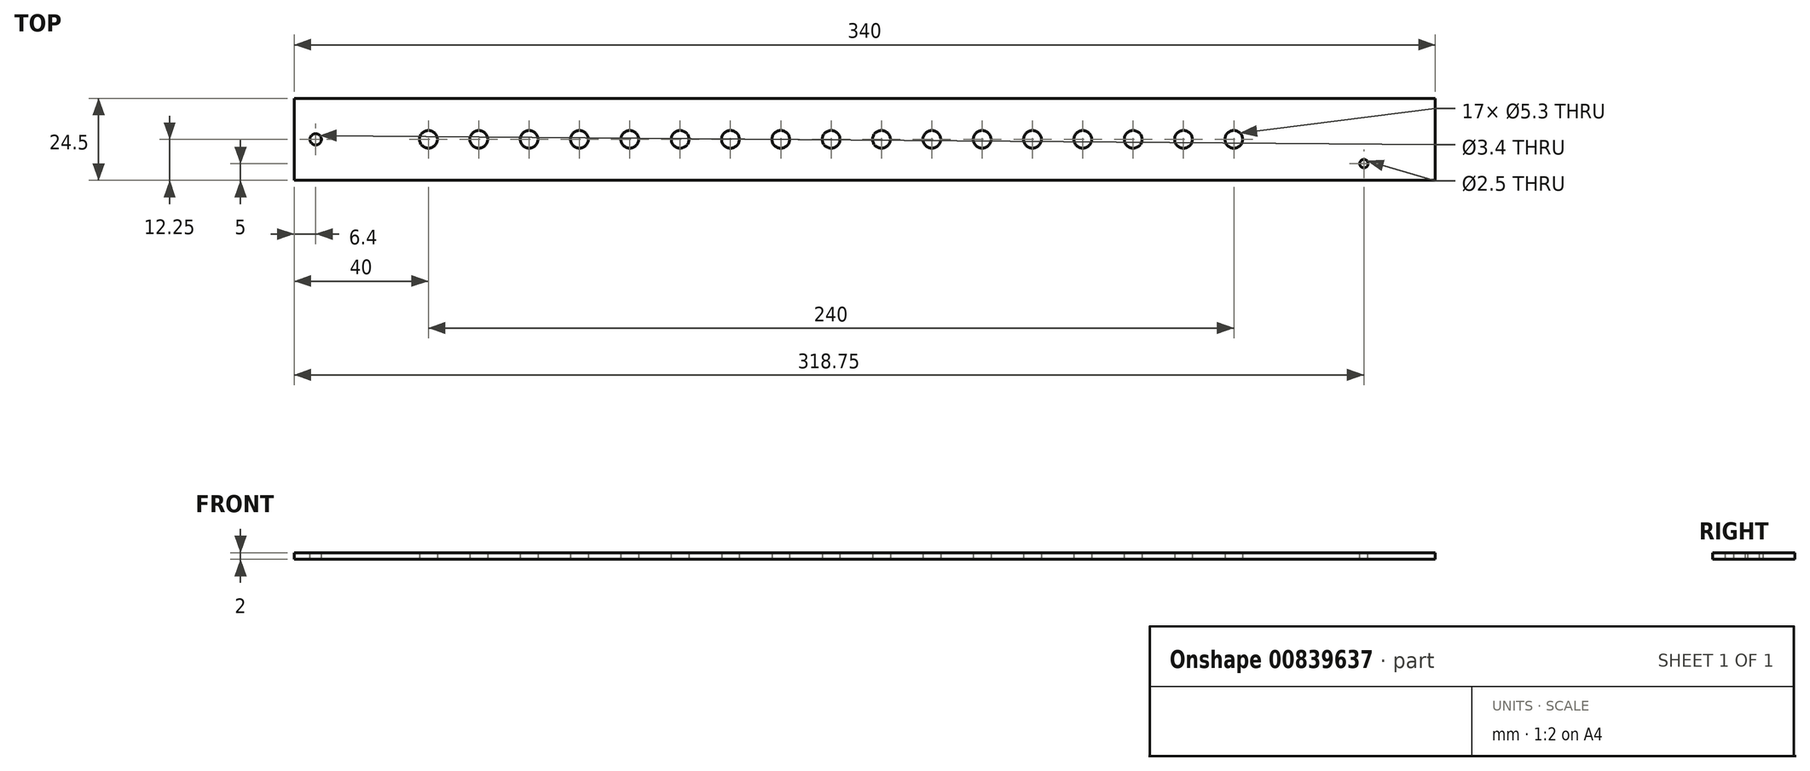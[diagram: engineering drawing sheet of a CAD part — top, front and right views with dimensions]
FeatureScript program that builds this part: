
annotation { "Feature Type Name" : "Feature", "Feature Type Description" : "" }
export const myFeature = defineFeature(function(context is Context, id is Id, definition is map)
    precondition{}
    {
        {
            var Q0;
            Q0=qCreatedBy(makeId("Top.planeOp"),FACE);
            var sketch = newSketch(context, id + "F0", { "sketchPlane" : qUnion([Q0])});
            skLineSegment(sketch, "E0.bottom", {"start": v(150, -12.25) * mm, "end": v(-150, -12.25) * mm});
            skLineSegment(sketch, "E0.top", {"start": v(150, 12.25) * mm, "end": v(-150, 12.25) * mm});
            skLineSegment(sketch, "E0.left", {"start": v(150, -12.25) * mm, "end": v(150, 12.25) * mm});
            skLineSegment(sketch, "E0.right", {"start": v(-150, -12.25) * mm, "end": v(-150, 12.25) * mm});
            skPoint(sketch, "E0.middle", {"position": v(0, 0) * mm});
            skCircle(sketch, "E1.1.0.0", {"center": v(-120, 0) * mm, "radius": 2.65 * mm});
            skCircle(sketch, "E1.2.0.0", {"center": v(-105, 0) * mm, "radius": 2.65 * mm});
            skCircle(sketch, "E1.3.0.0", {"center": v(-90, 0) * mm, "radius": 2.65 * mm});
            skCircle(sketch, "E1.4.0.0", {"center": v(-75, 0) * mm, "radius": 2.65 * mm});
            skCircle(sketch, "E1.5.0.0", {"center": v(-60, 0) * mm, "radius": 2.65 * mm});
            skCircle(sketch, "E1.6.0.0", {"center": v(-45, 0) * mm, "radius": 2.65 * mm});
            skCircle(sketch, "E1.7.0.0", {"center": v(-30, 0) * mm, "radius": 2.65 * mm});
            skCircle(sketch, "E1.8.0.0", {"center": v(-15, 0) * mm, "radius": 2.65 * mm});
            skCircle(sketch, "E1.9.0.0", {"center": v(0, 0) * mm, "radius": 2.65 * mm});
            skCircle(sketch, "E1.10.0.0", {"center": v(15, 0) * mm, "radius": 2.65 * mm});
            skCircle(sketch, "E1.11.0.0", {"center": v(30, 0) * mm, "radius": 2.65 * mm});
            skCircle(sketch, "E1.12.0.0", {"center": v(45, 0) * mm, "radius": 2.65 * mm});
            skCircle(sketch, "E1.13.0.0", {"center": v(60, 0) * mm, "radius": 2.65 * mm});
            skCircle(sketch, "E1.14.0.0", {"center": v(75, 0) * mm, "radius": 2.65 * mm});
            skCircle(sketch, "E1.15.0.0", {"center": v(90, 0) * mm, "radius": 2.65 * mm});
            skCircle(sketch, "E1.16.0.0", {"center": v(105, 0) * mm, "radius": 2.65 * mm});
            skCircle(sketch, "E1.17.0.0", {"center": v(120, 0) * mm, "radius": 2.65 * mm});
            skLineSegment(sketch, "E1.direction1", {"start": v(-135, 0) * mm, "end": v(-120, 0) * mm, "construction": true});
            skSolve(sketch);
        }
        {
            var Q0;
            Q0=makeQuery(id+"F0.imprint","IMPRINT",FACE,{"disambiguationData":[TD([[makeQuery(id+"F0.imprint","IMPRINT",EDGE,{"derivedFrom":sQuery(id+"F0.wireOp",EDGE,"E0.bottom")}),-1.0]])]});
            extrude(context, id + "F1", {"entities" : qUnion([Q0]), "depth" : 2 * mm, "offsetDistance" : 25 * mm});
        }
        {
            var Q0;
            Q0=makeQuery(id+"F1.opExtrude","SWEPT_FACE",FACE,{"disambiguationData":[OSD([sQuery(id+"F0.wireOp",EDGE,"E0.right")])]});
            extrude(context, id + "F2", {"entities" : qUnion([Q0]), "operationType" : NewBodyOperationType.ADD, "depth" : 10 * mm, "offsetDistance" : 25 * mm});
        }
        {
            var Q0;
            Q0=makeQuery(id+"F1.opExtrude","SWEPT_FACE",FACE,{"disambiguationData":[OSD([sQuery(id+"F0.wireOp",EDGE,"E0.left")])]});
            extrude(context, id + "F3", {"entities" : qUnion([Q0]), "operationType" : NewBodyOperationType.ADD, "depth" : 30 * mm, "offsetDistance" : 25 * mm});
        }
        {
            var Q0;
            {var subQ0=sQuery(id+"F0.wireOp",EDGE,"E0.left");var subQ1=sQuery(id+"F0.wireOp",EDGE,"E0.right");Q0=makeQuery(id+"F3.boolean.opBoolean","MERGE",FACE,{"derivedFrom":[makeQuery(id+"F2.boolean.opBoolean","MERGE",FACE,{"derivedFrom":[makeQuery(id+"F1.opExtrude","CAP_FACE",FACE,{"disambiguationData":[OSD([sQuery(id+"F0.wireOp",EDGE,"E0.bottom"),sQuery(id+"F0.wireOp",EDGE,"E0.top"),subQ0,subQ1,sQuery(id+"F0.wireOp",EDGE,"LckrCdrf-Oz9b-iWqB-HkfW-gHpTPrbceAxr"),sQuery(id+"F0.wireOp",EDGE,"E1.1.0.0"),sQuery(id+"F0.wireOp",EDGE,"E1.2.0.0"),sQuery(id+"F0.wireOp",EDGE,"E1.3.0.0"),sQuery(id+"F0.wireOp",EDGE,"E1.4.0.0"),sQuery(id+"F0.wireOp",EDGE,"E1.5.0.0"),sQuery(id+"F0.wireOp",EDGE,"E1.6.0.0"),sQuery(id+"F0.wireOp",EDGE,"E1.7.0.0"),sQuery(id+"F0.wireOp",EDGE,"E1.8.0.0"),sQuery(id+"F0.wireOp",EDGE,"E1.9.0.0"),sQuery(id+"F0.wireOp",EDGE,"E1.10.0.0"),sQuery(id+"F0.wireOp",EDGE,"E1.11.0.0"),sQuery(id+"F0.wireOp",EDGE,"E1.12.0.0"),sQuery(id+"F0.wireOp",EDGE,"E1.13.0.0"),sQuery(id+"F0.wireOp",EDGE,"E1.14.0.0"),sQuery(id+"F0.wireOp",EDGE,"E1.15.0.0"),sQuery(id+"F0.wireOp",EDGE,"E1.16.0.0"),sQuery(id+"F0.wireOp",EDGE,"E1.17.0.0"),sQuery(id+"F0.wireOp",EDGE,"E1.18.0.0")])],"isStart":false}),makeQuery(id+"F2.opExtrude","SWEPT_FACE",FACE,{"disambiguationData":[OSD([subQ1]),TDD([makeQuery(id+"F1.opExtrude","CAP_EDGE",EDGE,{"disambiguationData":[OSD([subQ1])],"isStart":false})])]})]}),makeQuery(id+"F3.opExtrude","SWEPT_FACE",FACE,{"disambiguationData":[OSD([subQ0]),TDD([makeQuery(id+"F1.opExtrude","CAP_EDGE",EDGE,{"disambiguationData":[OSD([subQ0])],"isStart":false})])]})]});}
            var sketch = newSketch(context, id + "F4", { "sketchPlane" : qUnion([Q0])});
            skCircle(sketch, "E2", {"center": v(-153.6, 0) * mm, "radius": 1.7 * mm});
            skSolve(sketch);
        }
        {
            var Q0;
            Q0=makeQuery(id+"F4.imprint","IMPRINT",FACE,{"disambiguationData":[TD([[makeQuery(id+"F4.imprint","IMPRINT",EDGE,{"derivedFrom":sQuery(id+"F4.wireOp",EDGE,"E2")}),1.0]])]});
            extrude(context, id + "F5", {"entities" : qUnion([Q0]), "operationType" : NewBodyOperationType.REMOVE, "endBound" : BoundingType.UP_TO_NEXT, "oppositeDirection" : true, "depth" : 25 * mm, "offsetDistance" : 25 * mm});
        }
        {
            var Q0;
            {var subQ0=sQuery(id+"F0.wireOp",EDGE,"E0.left");var subQ1=sQuery(id+"F0.wireOp",EDGE,"E0.right");Q0=makeQuery(id+"F3.boolean.opBoolean","MERGE",FACE,{"derivedFrom":[makeQuery(id+"F2.boolean.opBoolean","MERGE",FACE,{"derivedFrom":[makeQuery(id+"F1.opExtrude","CAP_FACE",FACE,{"disambiguationData":[OSD([sQuery(id+"F0.wireOp",EDGE,"E0.bottom"),sQuery(id+"F0.wireOp",EDGE,"E0.top"),subQ0,subQ1,sQuery(id+"F0.wireOp",EDGE,"LckrCdrf-Oz9b-iWqB-HkfW-gHpTPrbceAxr"),sQuery(id+"F0.wireOp",EDGE,"E1.1.0.0"),sQuery(id+"F0.wireOp",EDGE,"E1.2.0.0"),sQuery(id+"F0.wireOp",EDGE,"E1.3.0.0"),sQuery(id+"F0.wireOp",EDGE,"E1.4.0.0"),sQuery(id+"F0.wireOp",EDGE,"E1.5.0.0"),sQuery(id+"F0.wireOp",EDGE,"E1.6.0.0"),sQuery(id+"F0.wireOp",EDGE,"E1.7.0.0"),sQuery(id+"F0.wireOp",EDGE,"E1.8.0.0"),sQuery(id+"F0.wireOp",EDGE,"E1.9.0.0"),sQuery(id+"F0.wireOp",EDGE,"E1.10.0.0"),sQuery(id+"F0.wireOp",EDGE,"E1.11.0.0"),sQuery(id+"F0.wireOp",EDGE,"E1.12.0.0"),sQuery(id+"F0.wireOp",EDGE,"E1.13.0.0"),sQuery(id+"F0.wireOp",EDGE,"E1.14.0.0"),sQuery(id+"F0.wireOp",EDGE,"E1.15.0.0"),sQuery(id+"F0.wireOp",EDGE,"E1.16.0.0"),sQuery(id+"F0.wireOp",EDGE,"E1.17.0.0"),sQuery(id+"F0.wireOp",EDGE,"E1.18.0.0")])],"isStart":false}),makeQuery(id+"F2.opExtrude","SWEPT_FACE",FACE,{"disambiguationData":[OSD([subQ1]),TDD([makeQuery(id+"F1.opExtrude","CAP_EDGE",EDGE,{"disambiguationData":[OSD([subQ1])],"isStart":false})])]})]}),makeQuery(id+"F3.opExtrude","SWEPT_FACE",FACE,{"disambiguationData":[OSD([subQ0]),TDD([makeQuery(id+"F1.opExtrude","CAP_EDGE",EDGE,{"disambiguationData":[OSD([subQ0])],"isStart":false})])]})]});}
            var sketch = newSketch(context, id + "F6", { "sketchPlane" : qUnion([Q0])});
            skCircle(sketch, "E3", {"center": v(158.75, -7.25) * mm, "radius": 1.25 * mm});
            skSolve(sketch);
        }
        {
            var Q0;
            Q0=makeQuery(id+"F6.imprint","IMPRINT",FACE,{"disambiguationData":[TD([[makeQuery(id+"F6.imprint","IMPRINT",EDGE,{"derivedFrom":sQuery(id+"F6.wireOp",EDGE,"E3")}),1.0]])]});
            extrude(context, id + "F7", {"entities" : qUnion([Q0]), "operationType" : NewBodyOperationType.REMOVE, "endBound" : BoundingType.UP_TO_NEXT, "oppositeDirection" : true, "depth" : 25 * mm, "offsetDistance" : 25 * mm});
        }
    });
